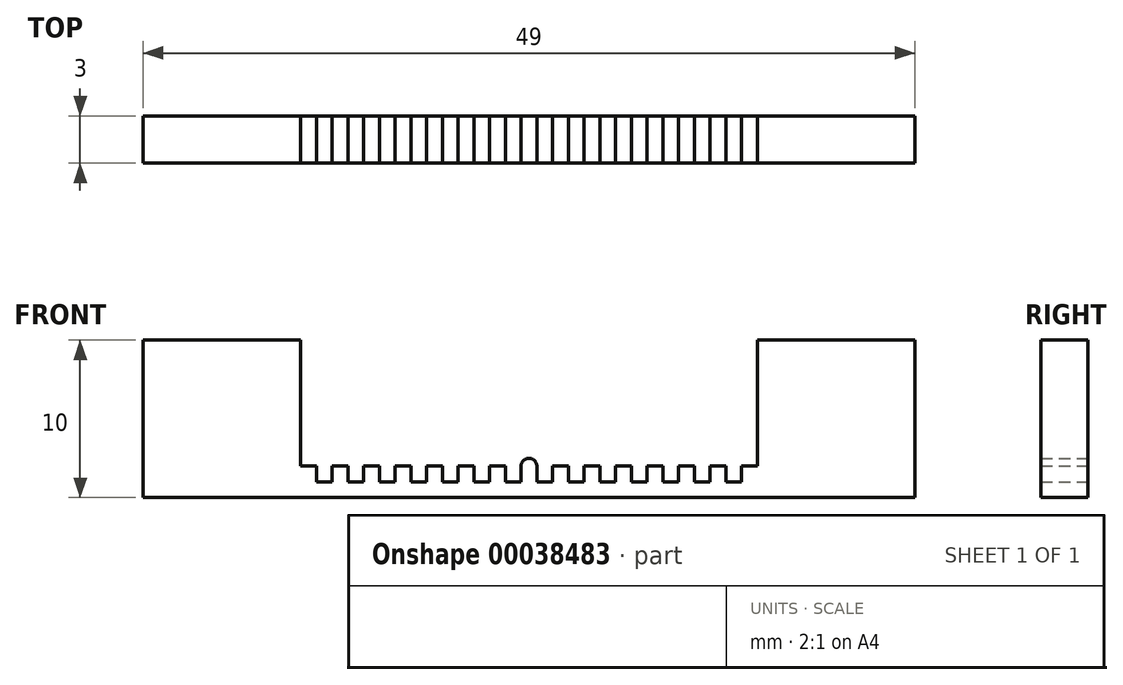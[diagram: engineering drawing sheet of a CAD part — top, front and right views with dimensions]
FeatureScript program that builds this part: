
annotation { "Feature Type Name" : "Feature", "Feature Type Description" : "" }
export const myFeature = defineFeature(function(context is Context, id is Id, definition is map)
    precondition{}
    {
        {
            var Q0;
            Q0=qCreatedBy(makeId("Front.planeOp"),FACE);
            var sketch = newSketch(context, id + "F0", { "sketchPlane" : qUnion([Q0])});
            skLineSegment(sketch, "E0.bottom", {"start": v(-57.75, 0) * mm, "end": v(-28.75, 0) * mm});
            skLineSegment(sketch, "E0.top", {"start": v(-57.75, 1) * mm, "end": v(-28.75, 1) * mm});
            skLineSegment(sketch, "E0.left", {"start": v(-57.75, 0) * mm, "end": v(-57.75, 1) * mm});
            skLineSegment(sketch, "E0.right", {"start": v(-28.75, 0) * mm, "end": v(-28.75, 1) * mm});
            skLineSegment(sketch, "E1.bottom", {"start": v(-57.75, 1) * mm, "end": v(-56.75, 1) * mm});
            skLineSegment(sketch, "E1.top", {"start": v(-57.75, 2) * mm, "end": v(-56.75, 2) * mm});
            skLineSegment(sketch, "E1.left", {"start": v(-57.75, 1) * mm, "end": v(-57.75, 2) * mm});
            skLineSegment(sketch, "E1.right", {"start": v(-56.75, 1) * mm, "end": v(-56.75, 2) * mm});
            skLineSegment(sketch, "E2.1.0.0", {"start": v(-55.75, 2) * mm, "end": v(-54.75, 2) * mm});
            skLineSegment(sketch, "E2.1.0.1", {"start": v(-55.75, 1) * mm, "end": v(-54.75, 1) * mm});
            skLineSegment(sketch, "E2.1.0.2", {"start": v(-55.75, 1) * mm, "end": v(-55.75, 2) * mm});
            skLineSegment(sketch, "E2.1.0.3", {"start": v(-54.75, 1) * mm, "end": v(-54.75, 2) * mm});
            skLineSegment(sketch, "E2.2.0.0", {"start": v(-53.75, 2) * mm, "end": v(-52.75, 2) * mm});
            skLineSegment(sketch, "E2.2.0.1", {"start": v(-53.75, 1) * mm, "end": v(-52.75, 1) * mm});
            skLineSegment(sketch, "E2.2.0.2", {"start": v(-53.75, 1) * mm, "end": v(-53.75, 2) * mm});
            skLineSegment(sketch, "E2.2.0.3", {"start": v(-52.75, 1) * mm, "end": v(-52.75, 2) * mm});
            skLineSegment(sketch, "E2.3.0.0", {"start": v(-51.75, 2) * mm, "end": v(-50.75, 2) * mm});
            skLineSegment(sketch, "E2.3.0.1", {"start": v(-51.75, 1) * mm, "end": v(-50.75, 1) * mm});
            skLineSegment(sketch, "E2.3.0.2", {"start": v(-51.75, 1) * mm, "end": v(-51.75, 2) * mm});
            skLineSegment(sketch, "E2.3.0.3", {"start": v(-50.75, 1) * mm, "end": v(-50.75, 2) * mm});
            skLineSegment(sketch, "E2.4.0.0", {"start": v(-49.75, 2) * mm, "end": v(-48.75, 2) * mm});
            skLineSegment(sketch, "E2.4.0.1", {"start": v(-49.75, 1) * mm, "end": v(-48.75, 1) * mm});
            skLineSegment(sketch, "E2.4.0.2", {"start": v(-49.75, 1) * mm, "end": v(-49.75, 2) * mm});
            skLineSegment(sketch, "E2.4.0.3", {"start": v(-48.75, 1) * mm, "end": v(-48.75, 2) * mm});
            skLineSegment(sketch, "E2.5.0.0", {"start": v(-47.75, 2) * mm, "end": v(-46.75, 2) * mm});
            skLineSegment(sketch, "E2.5.0.1", {"start": v(-47.75, 1) * mm, "end": v(-46.75, 1) * mm});
            skLineSegment(sketch, "E2.5.0.2", {"start": v(-47.75, 1) * mm, "end": v(-47.75, 2) * mm});
            skLineSegment(sketch, "E2.5.0.3", {"start": v(-46.75, 1) * mm, "end": v(-46.75, 2) * mm});
            skLineSegment(sketch, "E2.6.0.0", {"start": v(-45.75, 2) * mm, "end": v(-44.75, 2) * mm});
            skLineSegment(sketch, "E2.6.0.1", {"start": v(-45.75, 1) * mm, "end": v(-44.75, 1) * mm});
            skLineSegment(sketch, "E2.6.0.2", {"start": v(-45.75, 1) * mm, "end": v(-45.75, 2) * mm});
            skLineSegment(sketch, "E2.6.0.3", {"start": v(-44.75, 1) * mm, "end": v(-44.75, 2) * mm});
            skLineSegment(sketch, "E2.7.0.0", {"start": v(-43.75, 2) * mm, "end": v(-42.75, 2) * mm});
            skLineSegment(sketch, "E2.7.0.1", {"start": v(-43.75, 1) * mm, "end": v(-42.75, 1) * mm});
            skLineSegment(sketch, "E2.7.0.2", {"start": v(-43.75, 1) * mm, "end": v(-43.75, 2) * mm});
            skLineSegment(sketch, "E2.7.0.3", {"start": v(-42.75, 1) * mm, "end": v(-42.75, 2) * mm});
            skLineSegment(sketch, "E2.8.0.0", {"start": v(-41.75, 2) * mm, "end": v(-40.75, 2) * mm});
            skLineSegment(sketch, "E2.8.0.1", {"start": v(-41.75, 1) * mm, "end": v(-40.75, 1) * mm});
            skLineSegment(sketch, "E2.8.0.2", {"start": v(-41.75, 1) * mm, "end": v(-41.75, 2) * mm});
            skLineSegment(sketch, "E2.8.0.3", {"start": v(-40.75, 1) * mm, "end": v(-40.75, 2) * mm});
            skLineSegment(sketch, "E2.9.0.0", {"start": v(-39.75, 2) * mm, "end": v(-38.75, 2) * mm});
            skLineSegment(sketch, "E2.9.0.1", {"start": v(-39.75, 1) * mm, "end": v(-38.75, 1) * mm});
            skLineSegment(sketch, "E2.9.0.2", {"start": v(-39.75, 1) * mm, "end": v(-39.75, 2) * mm});
            skLineSegment(sketch, "E2.9.0.3", {"start": v(-38.75, 1) * mm, "end": v(-38.75, 2) * mm});
            skLineSegment(sketch, "E2.10.0.0", {"start": v(-37.75, 2) * mm, "end": v(-36.75, 2) * mm});
            skLineSegment(sketch, "E2.10.0.1", {"start": v(-37.75, 1) * mm, "end": v(-36.75, 1) * mm});
            skLineSegment(sketch, "E2.10.0.2", {"start": v(-37.75, 1) * mm, "end": v(-37.75, 2) * mm});
            skLineSegment(sketch, "E2.10.0.3", {"start": v(-36.75, 1) * mm, "end": v(-36.75, 2) * mm});
            skLineSegment(sketch, "E2.11.0.0", {"start": v(-35.75, 2) * mm, "end": v(-34.75, 2) * mm});
            skLineSegment(sketch, "E2.11.0.1", {"start": v(-35.75, 1) * mm, "end": v(-34.75, 1) * mm});
            skLineSegment(sketch, "E2.11.0.2", {"start": v(-35.75, 1) * mm, "end": v(-35.75, 2) * mm});
            skLineSegment(sketch, "E2.11.0.3", {"start": v(-34.75, 1) * mm, "end": v(-34.75, 2) * mm});
            skLineSegment(sketch, "E2.12.0.0", {"start": v(-33.75, 2) * mm, "end": v(-32.75, 2) * mm});
            skLineSegment(sketch, "E2.12.0.1", {"start": v(-33.75, 1) * mm, "end": v(-32.75, 1) * mm});
            skLineSegment(sketch, "E2.12.0.2", {"start": v(-33.75, 1) * mm, "end": v(-33.75, 2) * mm});
            skLineSegment(sketch, "E2.12.0.3", {"start": v(-32.75, 1) * mm, "end": v(-32.75, 2) * mm});
            skLineSegment(sketch, "E2.13.0.0", {"start": v(-31.75, 2) * mm, "end": v(-30.75, 2) * mm});
            skLineSegment(sketch, "E2.13.0.1", {"start": v(-31.75, 1) * mm, "end": v(-30.75, 1) * mm});
            skLineSegment(sketch, "E2.13.0.2", {"start": v(-31.75, 1) * mm, "end": v(-31.75, 2) * mm});
            skLineSegment(sketch, "E2.13.0.3", {"start": v(-30.75, 1) * mm, "end": v(-30.75, 2) * mm});
            skLineSegment(sketch, "E2.14.0.0", {"start": v(-29.75, 2) * mm, "end": v(-28.75, 2) * mm});
            skLineSegment(sketch, "E2.14.0.1", {"start": v(-29.75, 1) * mm, "end": v(-28.75, 1) * mm});
            skLineSegment(sketch, "E2.14.0.2", {"start": v(-29.75, 1) * mm, "end": v(-29.75, 2) * mm});
            skLineSegment(sketch, "E2.14.0.3", {"start": v(-28.75, 1) * mm, "end": v(-28.75, 2) * mm});
            skLineSegment(sketch, "E2.direction1", {"start": v(-57.75, 2) * mm, "end": v(-55.75, 2) * mm, "construction": true});
            skLineSegment(sketch, "E3.bottom", {"start": v(-57.75, 0) * mm, "end": v(-67.75, 0) * mm});
            skLineSegment(sketch, "E3.top", {"start": v(-57.75, 10) * mm, "end": v(-67.75, 10) * mm});
            skLineSegment(sketch, "E3.left", {"start": v(-57.75, 0) * mm, "end": v(-57.75, 10) * mm});
            skLineSegment(sketch, "E3.right", {"start": v(-67.75, 0) * mm, "end": v(-67.75, 10) * mm});
            skLineSegment(sketch, "E4.bottom", {"start": v(-28.75, 0) * mm, "end": v(-18.75, 0) * mm});
            skLineSegment(sketch, "E4.top", {"start": v(-28.75, 10) * mm, "end": v(-18.75, 10) * mm});
            skLineSegment(sketch, "E4.left", {"start": v(-28.75, 0) * mm, "end": v(-28.75, 10) * mm});
            skLineSegment(sketch, "E4.right", {"start": v(-18.75, 0) * mm, "end": v(-18.75, 10) * mm});
            skArc(sketch, "E5", {"start": v(-42.75, 2) * mm, "mid": v(-43.25, 2.5) * mm, "end": v(-43.75, 2) * mm});
            skSolve(sketch);
        }
        {
            var Q0;
            Q0 = qSketchRegion(id + "F0", true);
            extrude(context, id + "F1", {"entities" : qUnion([Q0]), "depth" : 3 * mm});
        }
    });
